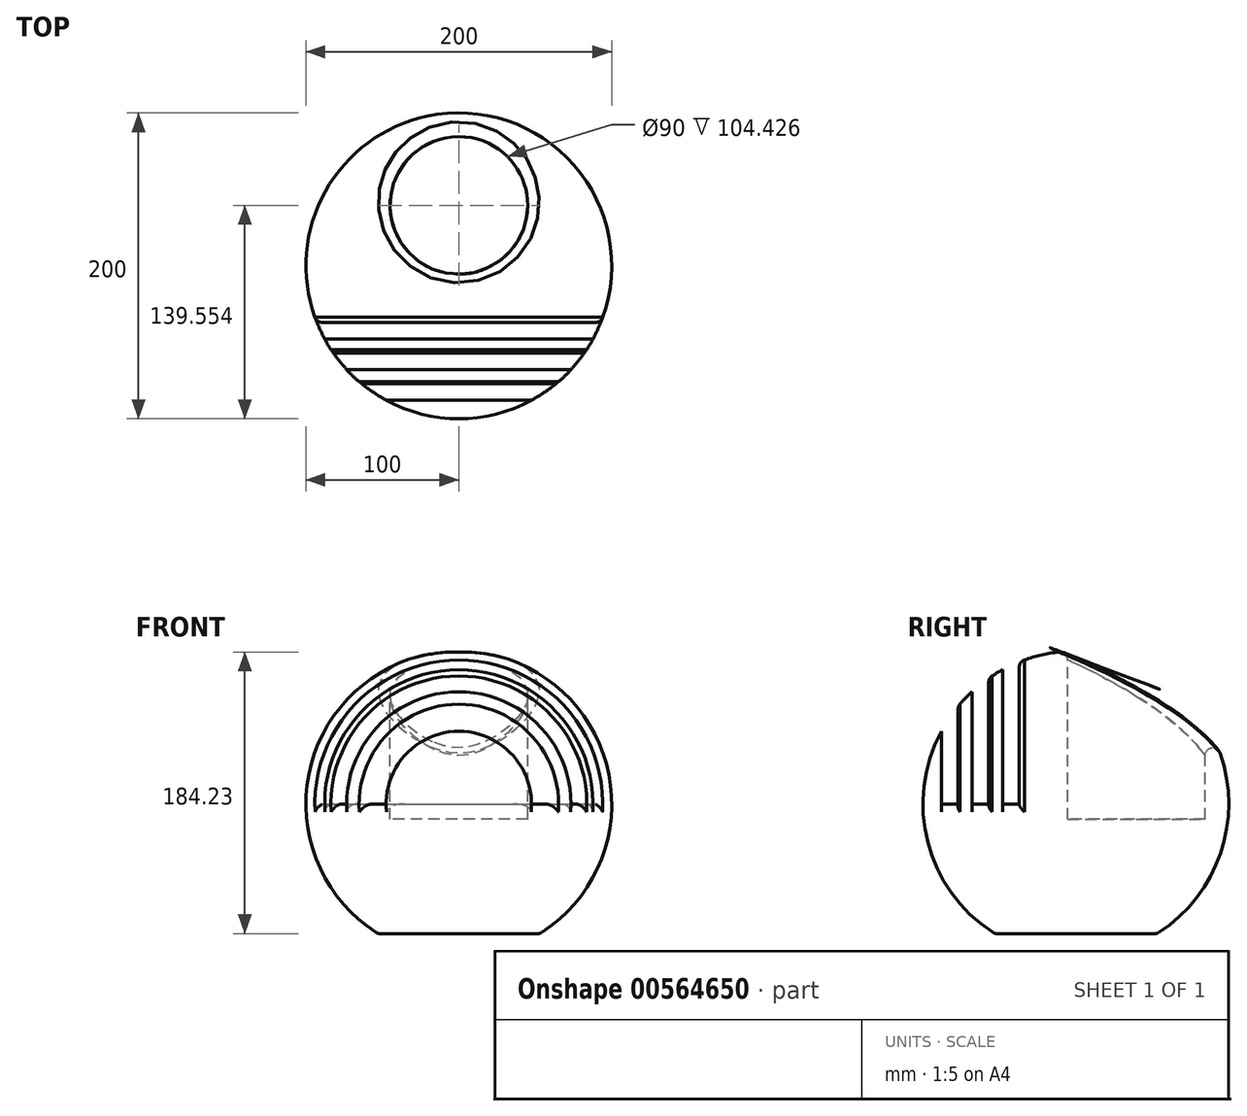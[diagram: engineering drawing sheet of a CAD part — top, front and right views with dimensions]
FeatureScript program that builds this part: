
annotation { "Feature Type Name" : "Feature", "Feature Type Description" : "" }
export const myFeature = defineFeature(function(context is Context, id is Id, definition is map)
    precondition{}
    {
        {
            var Q0;
            Q0=qCreatedBy(makeId("Front.planeOp"),FACE);
            var sketch = newSketch(context, id + "F0", { "sketchPlane" : qUnion([Q0])});
            skArc(sketch, "E0", {"start": v(0, -100) * mm, "mid": v(100, 0) * mm, "end": v(0, 100) * mm});
            skLineSegment(sketch, "E1", {"start": v(0, 100) * mm, "end": v(0, -100) * mm});
            skSolve(sketch);
        }
        {
            var Q0;
            Q0=makeQuery(id+"F0.imprint","IMPRINT",FACE,{"disambiguationData":[TD([[makeQuery(id+"F0.imprint","IMPRINT",EDGE,{"derivedFrom":sQuery(id+"F0.wireOp",EDGE,"E0")}),1.0]])]});
            var Q1;
            Q1=sQuery(id+"F0.wireOp",EDGE,"E1");
            revolve(context, id + "F1", {"entities" : qUnion([Q0]), "axis" : qUnion([Q1]), "revolveType" : RevolveType.FULL});
        }
        {
            var Q0;
            Q0=qCreatedBy(makeId("Top.planeOp"),FACE);
            var sketch = newSketch(context, id + "F2", { "sketchPlane" : qUnion([Q0])});
            skLineSegment(sketch, "E2.bottom", {"start": v(-117.56, -37) * mm, "end": v(117.03, -37) * mm});
            skLineSegment(sketch, "E2.top", {"start": v(-117.56, -48) * mm, "end": v(117.03, -48) * mm});
            skLineSegment(sketch, "E2.left", {"start": v(-117.56, -37) * mm, "end": v(-117.56, -48) * mm});
            skLineSegment(sketch, "E2.right", {"start": v(117.03, -37) * mm, "end": v(117.03, -48) * mm});
            skLineSegment(sketch, "E3.bottom", {"start": v(-110.24, -57) * mm, "end": v(106.23, -57) * mm});
            skLineSegment(sketch, "E3.top", {"start": v(-110.24, -68) * mm, "end": v(106.23, -68) * mm});
            skLineSegment(sketch, "E3.left", {"start": v(-110.24, -57) * mm, "end": v(-110.24, -68) * mm});
            skLineSegment(sketch, "E3.right", {"start": v(106.23, -57) * mm, "end": v(106.23, -68) * mm});
            skLineSegment(sketch, "E4.bottom", {"start": v(-75.27, -77) * mm, "end": v(76.5, -77) * mm});
            skLineSegment(sketch, "E4.top", {"start": v(-75.27, -88) * mm, "end": v(76.5, -88) * mm});
            skLineSegment(sketch, "E4.left", {"start": v(-75.27, -77) * mm, "end": v(-75.27, -88) * mm});
            skLineSegment(sketch, "E4.right", {"start": v(76.5, -77) * mm, "end": v(76.5, -88) * mm});
            skSolve(sketch);
        }
        {
            var Q0;
            Q0=makeQuery(id+"F2.imprint","IMPRINT",FACE,{"disambiguationData":[TD([[makeQuery(id+"F2.imprint","IMPRINT",EDGE,{"derivedFrom":sQuery(id+"F2.wireOp",EDGE,"IW6yeioO-STk1-u0uN-wqK1-MGAWKFEtwxE6.bottom")}),-1.0]])]});
            var Q1;
            Q1=makeQuery(id+"F2.imprint","IMPRINT",FACE,{"disambiguationData":[TD([[makeQuery(id+"F2.imprint","IMPRINT",EDGE,{"derivedFrom":sQuery(id+"F2.wireOp",EDGE,"eqWsPOYB-hsWt-IOIY-6PBg-MDbqaR3U2wcC.bottom")}),-1.0]])]});
            var Q2;
            Q2=makeQuery(id+"F2.imprint","IMPRINT",FACE,{"disambiguationData":[TD([[makeQuery(id+"F2.imprint","IMPRINT",EDGE,{"derivedFrom":sQuery(id+"F2.wireOp",EDGE,"E2.bottom")}),-1.0]])]});
            var Q3;
            Q3=makeQuery(id+"F2.imprint","IMPRINT",FACE,{"disambiguationData":[TD([[makeQuery(id+"F2.imprint","IMPRINT",EDGE,{"derivedFrom":sQuery(id+"F2.wireOp",EDGE,"E3.bottom")}),-1.0]])]});
            var Q4;
            Q4=makeQuery(id+"F2.imprint","IMPRINT",FACE,{"disambiguationData":[TD([[makeQuery(id+"F2.imprint","IMPRINT",EDGE,{"derivedFrom":sQuery(id+"F2.wireOp",EDGE,"E4.bottom")}),-1.0]])]});
            extrude(context, id + "F3", {"entities" : qUnion([Q0, Q1, Q2, Q3, Q4]), "operationType" : NewBodyOperationType.REMOVE, "depth" : 209 * mm, "offsetDistance" : 25 * mm});
        }
        {
            var Q0;
            Q0=qCreatedBy(makeId("Top.planeOp"),FACE);
            cPlane(context, id + "F4", {"entities" : qUnion([Q0]), "cplaneType" : CPlaneType.OFFSET, "offset" : 100 * mm, "width" : 150 * mm, "height" : 150 * mm});
        }
        {
            var Q0;
            Q0=qCreatedBy(id+"F4.planeOp",FACE);
            var sketch = newSketch(context, id + "F5", { "sketchPlane" : qUnion([Q0])});
            skCircle(sketch, "E5", {"center": v(0, 39.55) * mm, "radius": 45 * mm});
            skSolve(sketch);
        }
        {
            var Q0;
            Q0=qCreatedBy(makeId("Right.planeOp"),FACE);
            var sketch = newSketch(context, id + "F6", { "sketchPlane" : qUnion([Q0])});
            skLineSegment(sketch, "E6.bottom", {"start": v(-76.17, -84.81) * mm, "end": v(88.83, -84.81) * mm});
            skLineSegment(sketch, "E6.top", {"start": v(-76.17, -104.81) * mm, "end": v(88.83, -104.81) * mm});
            skLineSegment(sketch, "E6.left", {"start": v(-76.17, -84.81) * mm, "end": v(-76.17, -104.81) * mm});
            skLineSegment(sketch, "E6.right", {"start": v(88.83, -84.81) * mm, "end": v(88.83, -104.81) * mm});
            skSolve(sketch);
        }
        {
            var Q0;
            Q0=makeQuery(id+"F6.imprint","IMPRINT",FACE,{"disambiguationData":[TD([[makeQuery(id+"F6.imprint","IMPRINT",EDGE,{"derivedFrom":sQuery(id+"F6.wireOp",EDGE,"E6.bottom")}),-1.0]])]});
            extrude(context, id + "F7", {"entities" : qUnion([Q0]), "operationType" : NewBodyOperationType.REMOVE, "depth" : 126 * mm, "offsetDistance" : 25 * mm, "hasSecondDirection" : true, "secondDirectionOppositeDirection" : true, "secondDirectionDepth" : 99 * mm});
        }
        {
            var Q0;
            Q0=makeQuery(id+"F5.imprint","IMPRINT",FACE,{"disambiguationData":[TD([[makeQuery(id+"F5.imprint","IMPRINT",EDGE,{"derivedFrom":sQuery(id+"F5.wireOp",EDGE,"E5")}),1.0]])]});
            extrude(context, id + "F8", {"entities" : qUnion([Q0]), "operationType" : NewBodyOperationType.REMOVE, "oppositeDirection" : true, "depth" : 110 * mm, "offsetDistance" : 25 * mm});
        }
        {
            var Q0;
            Q0=makeQuery(id+"F8.boolean.opBoolean","INTERSECT",EDGE,{"derivedFrom":[makeQuery(id+"F1.opRevolve","SWEPT_FACE",FACE,{"disambiguationData":[OSD([sQuery(id+"F0.wireOp",EDGE,"E0")])]}),makeQuery(id+"F8.opExtrude","SWEPT_FACE",FACE,{"disambiguationData":[OSD([sQuery(id+"F5.wireOp",EDGE,"E5")])]})]});
            fillet(context, id + "F9", {"entities" : qUnion([Q0]), "radius" : 5 * mm, "tangentPropagation" : true, "allowEdgeOverflow" : false});
        }
        {
            var Q0;
            Q0=makeQuery(id+"F3.boolean.opBoolean","INTERSECT",EDGE,{"derivedFrom":[makeQuery(id+"F1.opRevolve","SWEPT_FACE",FACE,{"disambiguationData":[OSD([sQuery(id+"F0.wireOp",EDGE,"E0")])]}),makeQuery(id+"F3.opExtrude","SWEPT_FACE",FACE,{"disambiguationData":[OSD([sQuery(id+"F2.wireOp",EDGE,"E4.bottom")])]})]});
            var Q1;
            Q1=makeQuery(id+"F3.boolean.opBoolean","INTERSECT",EDGE,{"derivedFrom":[makeQuery(id+"F1.opRevolve","SWEPT_FACE",FACE,{"disambiguationData":[OSD([sQuery(id+"F0.wireOp",EDGE,"E0")])]}),makeQuery(id+"F3.opExtrude","SWEPT_FACE",FACE,{"disambiguationData":[OSD([sQuery(id+"F2.wireOp",EDGE,"E3.bottom")])]})]});
            var Q2;
            Q2=makeQuery(id+"F3.boolean.opBoolean","INTERSECT",EDGE,{"derivedFrom":[makeQuery(id+"F1.opRevolve","SWEPT_FACE",FACE,{"disambiguationData":[OSD([sQuery(id+"F0.wireOp",EDGE,"E0")])]}),makeQuery(id+"F3.opExtrude","SWEPT_FACE",FACE,{"disambiguationData":[OSD([sQuery(id+"F2.wireOp",EDGE,"E2.bottom")])]})]});
            var Q3;
            Q3=makeQuery(id+"F3.boolean.opBoolean","INTERSECT",EDGE,{"disambiguationData":[OD(0.0)],"derivedFrom":[makeQuery(id+"F1.opRevolve","SWEPT_FACE",FACE,{"disambiguationData":[OSD([sQuery(id+"F0.wireOp",EDGE,"E0")])]}),makeQuery(id+"F3.opExtrude","CAP_FACE",FACE,{"disambiguationData":[OSD([sQuery(id+"F2.wireOp",EDGE,"E2.bottom"),sQuery(id+"F2.wireOp",EDGE,"E2.top"),sQuery(id+"F2.wireOp",EDGE,"E2.left"),sQuery(id+"F2.wireOp",EDGE,"E2.right")])],"isStart":true})]});
            var Q4;
            Q4=makeQuery(id+"F3.boolean.opBoolean","INTERSECT",EDGE,{"disambiguationData":[OD(0.0)],"derivedFrom":[makeQuery(id+"F1.opRevolve","SWEPT_FACE",FACE,{"disambiguationData":[OSD([sQuery(id+"F0.wireOp",EDGE,"E0")])]}),makeQuery(id+"F3.opExtrude","CAP_FACE",FACE,{"disambiguationData":[OSD([sQuery(id+"F2.wireOp",EDGE,"E3.bottom"),sQuery(id+"F2.wireOp",EDGE,"E3.top"),sQuery(id+"F2.wireOp",EDGE,"E3.left"),sQuery(id+"F2.wireOp",EDGE,"E3.right")])],"isStart":true})]});
            var Q5;
            Q5=makeQuery(id+"F3.boolean.opBoolean","INTERSECT",EDGE,{"disambiguationData":[OD(0.0)],"derivedFrom":[makeQuery(id+"F1.opRevolve","SWEPT_FACE",FACE,{"disambiguationData":[OSD([sQuery(id+"F0.wireOp",EDGE,"E0")])]}),makeQuery(id+"F3.opExtrude","CAP_FACE",FACE,{"disambiguationData":[OSD([sQuery(id+"F2.wireOp",EDGE,"E4.bottom"),sQuery(id+"F2.wireOp",EDGE,"E4.top"),sQuery(id+"F2.wireOp",EDGE,"E4.left"),sQuery(id+"F2.wireOp",EDGE,"E4.right")])],"isStart":true})]});
            var Q6;
            Q6=makeQuery(id+"F3.boolean.opBoolean","INTERSECT",EDGE,{"disambiguationData":[OD(1.0)],"derivedFrom":[makeQuery(id+"F1.opRevolve","SWEPT_FACE",FACE,{"disambiguationData":[OSD([sQuery(id+"F0.wireOp",EDGE,"E0")])]}),makeQuery(id+"F3.opExtrude","CAP_FACE",FACE,{"disambiguationData":[OSD([sQuery(id+"F2.wireOp",EDGE,"E2.bottom"),sQuery(id+"F2.wireOp",EDGE,"E2.top"),sQuery(id+"F2.wireOp",EDGE,"E2.left"),sQuery(id+"F2.wireOp",EDGE,"E2.right")])],"isStart":true})]});
            var Q7;
            Q7=makeQuery(id+"F3.boolean.opBoolean","INTERSECT",EDGE,{"disambiguationData":[OD(1.0)],"derivedFrom":[makeQuery(id+"F1.opRevolve","SWEPT_FACE",FACE,{"disambiguationData":[OSD([sQuery(id+"F0.wireOp",EDGE,"E0")])]}),makeQuery(id+"F3.opExtrude","CAP_FACE",FACE,{"disambiguationData":[OSD([sQuery(id+"F2.wireOp",EDGE,"E3.bottom"),sQuery(id+"F2.wireOp",EDGE,"E3.top"),sQuery(id+"F2.wireOp",EDGE,"E3.left"),sQuery(id+"F2.wireOp",EDGE,"E3.right")])],"isStart":true})]});
            var Q8;
            Q8=makeQuery(id+"F3.boolean.opBoolean","INTERSECT",EDGE,{"disambiguationData":[OD(1.0)],"derivedFrom":[makeQuery(id+"F1.opRevolve","SWEPT_FACE",FACE,{"disambiguationData":[OSD([sQuery(id+"F0.wireOp",EDGE,"E0")])]}),makeQuery(id+"F3.opExtrude","CAP_FACE",FACE,{"disambiguationData":[OSD([sQuery(id+"F2.wireOp",EDGE,"E4.bottom"),sQuery(id+"F2.wireOp",EDGE,"E4.top"),sQuery(id+"F2.wireOp",EDGE,"E4.left"),sQuery(id+"F2.wireOp",EDGE,"E4.right")])],"isStart":true})]});
            fillet(context, id + "F10", {"entities" : qUnion([Q0, Q1, Q2, Q3, Q4, Q5, Q6, Q7, Q8]), "radius" : 5 * mm, "allowEdgeOverflow" : false});
        }
        {
            var Q0;
            Q0=makeQuery(id+"F7.boolean.opBoolean","INTERSECT",EDGE,{"derivedFrom":[makeQuery(id+"F1.opRevolve","SWEPT_FACE",FACE,{"disambiguationData":[OSD([sQuery(id+"F0.wireOp",EDGE,"E0")])]}),makeQuery(id+"F7.opExtrude","SWEPT_FACE",FACE,{"disambiguationData":[OSD([sQuery(id+"F6.wireOp",EDGE,"E6.bottom")])]})]});
            fillet(context, id + "F11", {"entities" : qUnion([Q0]), "radius" : 5 * mm, "tangentPropagation" : true, "allowEdgeOverflow" : false});
        }
    });
